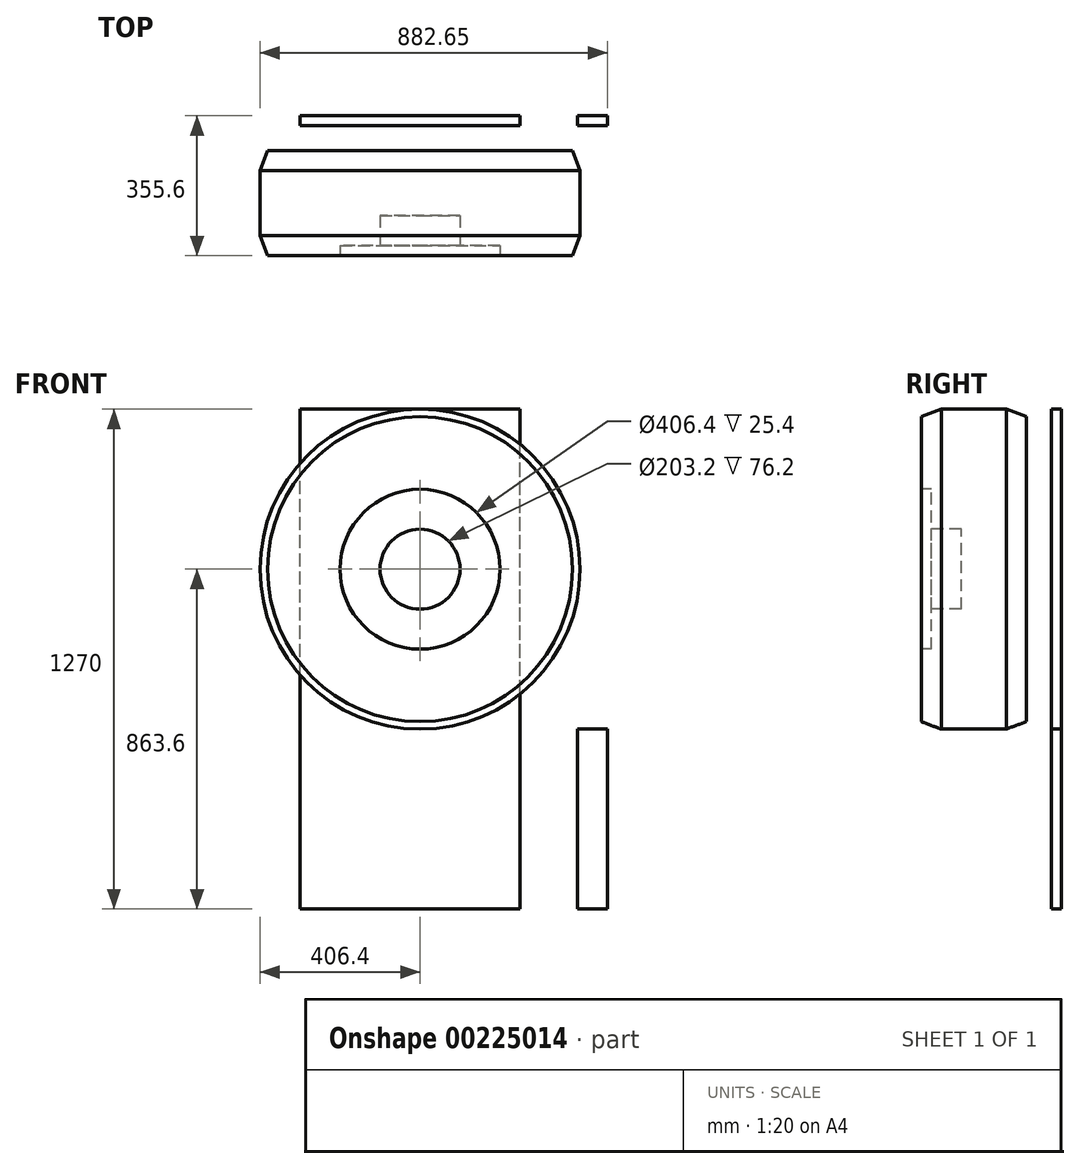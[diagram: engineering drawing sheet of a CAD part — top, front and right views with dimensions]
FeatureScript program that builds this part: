
annotation { "Feature Type Name" : "Feature", "Feature Type Description" : "" }
export const myFeature = defineFeature(function(context is Context, id is Id, definition is map)
    precondition{}
    {
        {
            var Q0;
            Q0=qCreatedBy(makeId("Front.planeOp"),FACE);
            var sketch = newSketch(context, id + "F0", { "sketchPlane" : qUnion([Q0])});
            skLineSegment(sketch, "E0.bottom", {"start": v(0, 0) * mm, "end": v(558.8, 0) * mm});
            skLineSegment(sketch, "E0.top", {"start": v(0, 1270) * mm, "end": v(558.8, 1270) * mm});
            skLineSegment(sketch, "E0.left", {"start": v(0, 0) * mm, "end": v(0, 1270) * mm});
            skLineSegment(sketch, "E0.right", {"start": v(558.8, 0) * mm, "end": v(558.8, 1270) * mm});
            skLineSegment(sketch, "E1.bottom", {"start": v(565.15, 0) * mm, "end": v(781.05, 0) * mm});
            skLineSegment(sketch, "E1.top", {"start": v(565.15, 1371.6) * mm, "end": v(781.05, 1371.6) * mm});
            skLineSegment(sketch, "E1.left", {"start": v(565.15, 0) * mm, "end": v(565.15, 1371.6) * mm});
            skLineSegment(sketch, "E1.right", {"start": v(781.05, 0) * mm, "end": v(781.05, 1371.6) * mm});
            skLineSegment(sketch, "E2.bottom", {"start": v(781.05, 0) * mm, "end": v(704.85, 0) * mm});
            skLineSegment(sketch, "E2.top", {"start": v(781.05, 457.2) * mm, "end": v(704.85, 457.2) * mm});
            skLineSegment(sketch, "E2.left", {"start": v(781.05, 0) * mm, "end": v(781.05, 457.2) * mm});
            skLineSegment(sketch, "E2.right", {"start": v(704.85, 0) * mm, "end": v(704.85, 457.2) * mm});
            skSolve(sketch);
        }
        {
            var Q0;
            Q0=makeQuery(id+"F0.imprint","IMPRINT",FACE,{"disambiguationData":[TD([[makeQuery(id+"F0.imprint","IMPRINT",EDGE,{"derivedFrom":sQuery(id+"F0.wireOp",EDGE,"E0.bottom")}),1.0]])]});
            var Q1;
            Q1=makeQuery(id+"F0.imprint","IMPRINT",FACE,{"disambiguationData":[TD([[makeQuery(id+"F0.imprint","IMPRINT",EDGE,{"derivedFrom":sQuery(id+"F0.wireOp",EDGE,"E1.bottom")}),1.0]])]});
            extrude(context, id + "F1", {"entities" : qUnion([Q0, Q1]), "oppositeDirection" : true, "depth" : 25.4 * mm, "offsetDistance" : 25.4 * mm});
        }
        {
            var Q0;
            Q0=qCreatedBy(makeId("Front.planeOp"),FACE);
            var sketch = newSketch(context, id + "F2", { "sketchPlane" : qUnion([Q0])});
            skCircle(sketch, "E3", {"center": v(304.8, 863.6) * mm, "radius": 406.4 * mm});
            skSolve(sketch);
        }
        {
            var Q0;
            Q0=makeQuery(id+"F2.imprint","IMPRINT",FACE,{"disambiguationData":[TD([[makeQuery(id+"F2.imprint","IMPRINT",EDGE,{"derivedFrom":sQuery(id+"F2.wireOp",EDGE,"E3")}),1.0]])]});
            extrude(context, id + "F3", {"entities" : qUnion([Q0]), "depth" : 330.2 * mm, "offsetDistance" : 25.4 * mm, "hasSecondDirection" : true, "secondDirectionOppositeDirection" : false, "secondDirectionDepth" : 63.5 * mm});
        }
        {
            var Q0;
            Q0=makeQuery(id+"F3.opExtrude","CAP_FACE",FACE,{"disambiguationData":[OSD([sQuery(id+"F2.wireOp",EDGE,"E3")])],"isStart":false});
            var Q1;
            Q1=makeQuery(id+"F3.opExtrude","CAP_EDGE",EDGE,{"disambiguationData":[OSD([sQuery(id+"F2.wireOp",EDGE,"E3")])],"isStart":true});
            chamfer(context, id + "F4", {"entities" : qUnion([Q0, Q1]), "chamferType" : ChamferType.TWO_OFFSETS, "width1" : 50.8 * mm, "oppositeDirection" : false, "width2" : 19.05 * mm, "tangentPropagation" : true});
        }
        {
            var Q0;
            Q0=makeQuery(id+"F3.opExtrude","CAP_FACE",FACE,{"disambiguationData":[OSD([sQuery(id+"F2.wireOp",EDGE,"E3")])],"isStart":false});
            var sketch = newSketch(context, id + "F5", { "sketchPlane" : qUnion([Q0])});
            skCircle(sketch, "E4", {"center": v(304.8, 863.6) * mm, "radius": 203.2 * mm});
            skSolve(sketch);
        }
        {
            var Q0;
            Q0=makeQuery(id+"F5.imprint","IMPRINT",FACE,{"disambiguationData":[TD([[makeQuery(id+"F5.imprint","IMPRINT",EDGE,{"derivedFrom":sQuery(id+"F5.wireOp",EDGE,"E4")}),1.0]])]});
            extrude(context, id + "F6", {"entities" : qUnion([Q0]), "operationType" : NewBodyOperationType.REMOVE, "oppositeDirection" : true, "depth" : 25.4 * mm, "offsetDistance" : 25.4 * mm});
        }
        {
            var Q0;
            Q0=makeQuery(id+"F6.boolean.opBoolean","COPY",FACE,{"derivedFrom":makeQuery(id+"F6.opExtrude","CAP_FACE",FACE,{"disambiguationData":[OSD([sQuery(id+"F5.wireOp",EDGE,"E4")])],"isStart":false})});
            var sketch = newSketch(context, id + "F7", { "sketchPlane" : qUnion([Q0])});
            skCircle(sketch, "E5", {"center": v(304.8, 863.6) * mm, "radius": 101.6 * mm});
            skSolve(sketch);
        }
        {
            var Q0;
            Q0=makeQuery(id+"F7.imprint","IMPRINT",FACE,{"disambiguationData":[TD([[makeQuery(id+"F7.imprint","IMPRINT",EDGE,{"derivedFrom":sQuery(id+"F7.wireOp",EDGE,"E5")}),1.0]])]});
            extrude(context, id + "F8", {"entities" : qUnion([Q0]), "operationType" : NewBodyOperationType.REMOVE, "oppositeDirection" : true, "depth" : 76.2 * mm, "offsetDistance" : 25.4 * mm});
        }
    });
